# Revit family: LAMP_AMBIENT
name_source: partatom
category: Modelos genéricos
revit_build: Autodesk Revit 2015 (Build: 20140606_1530(x64)
units: mm (PartAtom-declared; Revit-internal decimal feet)

## types (8) — shared parameters
CRI = 80
Elevación por defecto = 1219 mm
Fabricante = LAMP
Gear = Electronic
IEE = A++
Installation instructions = https://www.lamp.es
Insulation class = I
LED Lifetime = 50.000 L80 B10
Lamp = MID-POWER LED
Last update = 15/05/2020
Luminaire type = Indoor - Wall Mounted
MacAdam = 3
Manufacturer URL = http://www.lamp.es
Manufacturer country = Spain
Manufacturer name = LAMP
Photometric web file = Cuerpo ambient : 1950LM 3000 700MM GREY
Power Supply = 220-240V 50-60Hz
Product URL = https://www.lamp.es
Product datasheet = http://www.lamp.es
Protection rating = IP40
Type = MID POWER TRIDONIC

## per-type parameters (varying)
| type | Descripción | Dimensions | Efficacy | Finish | Initial color | Initial intensity | Modelo | Plum | Power | Product code | Weight |
| 1950LM 3000 700MM WHITE | AMBIENT LED 700MM 2600 WW WH. | 700 x 108 x 75 | 104 lm/W | Matte white | 3000 K | 1950 lm | AM1WM07015830NW | 19 W | 16 W | AM1WM07015830NW | 1.66 kg |
| 1950LM 3000 700MM GREY | AMBIENT LED 700MM 2600 WW GR. | 700 x 108 x 75 | 104 lm/W | Gloss grey | 3000 K | 1950 lm | AM1WM07015830NG | 19 W | 16 W | AM1WM07015830NG | 1.66 kg |
| 2030LM 4000 700MM WHITE | AMBIENT LED 700MM 2600 NW WH. | 700 x 108 x 75 | 108 lm/W | Matte white | 4000 K | 2030 lm | AM1WM07015840NW | 19 W | 16 W | AM1WM07015840NW | 1.66 kg |
| 2030LM 4000 700MM GREY | AMBIENT LED 700MM 2600 NW GR. | 700 x 108 x 75 | 108 lm/W | Gloss grey | 4000 K | 2030 lm | AM1WM07015840NG | 19 W | 16 W | AM1WM07015840NG | 1.66 kg |
| 3900LM 3000 1300MM WHITE | AMBIENT LED 1300MM 5200 WW WH. | 1300 x 108 x 75 | 111 lm/W | Matte white | 3000 K | 3900 lm | AM1WM13015830NW | 35 W | 31 W | AM1WM13015830NW | 2.99 kg |
| 3900LM 3000 1300MM GREY | AMBIENT LED 1300MM 5200 WW GR. | 1300 x 108 x 75 | 111 lm/W | Gloss grey | 3000 K | 3900 lm | AM1WM13015830NG | 35 W | 31 W | AM1WM13015830NG | 2.99 kg |
| 4060LM 4000 1300MM WHITE | AMBIENT LED 1300MM 5200 NW WH. | 1300 x 108 x 75 | 116 lm/W | Matte white | 4000 K | 4060 lm | AM1WM13015840NW | 35 W | 31 W | AM1WM13015840NW | 2.99 kg |
| 4060LM 4000 1300MM GREY | AMBIENT LED 1300MM 5200 NW GR. | 1300 x 108 x 75 | 116 lm/W | Gloss grey | 4000 K | 4060 lm | AM1WM13015840NG | 35 W | 31 W | AM1WM13015840NG | 2.99 kg |
